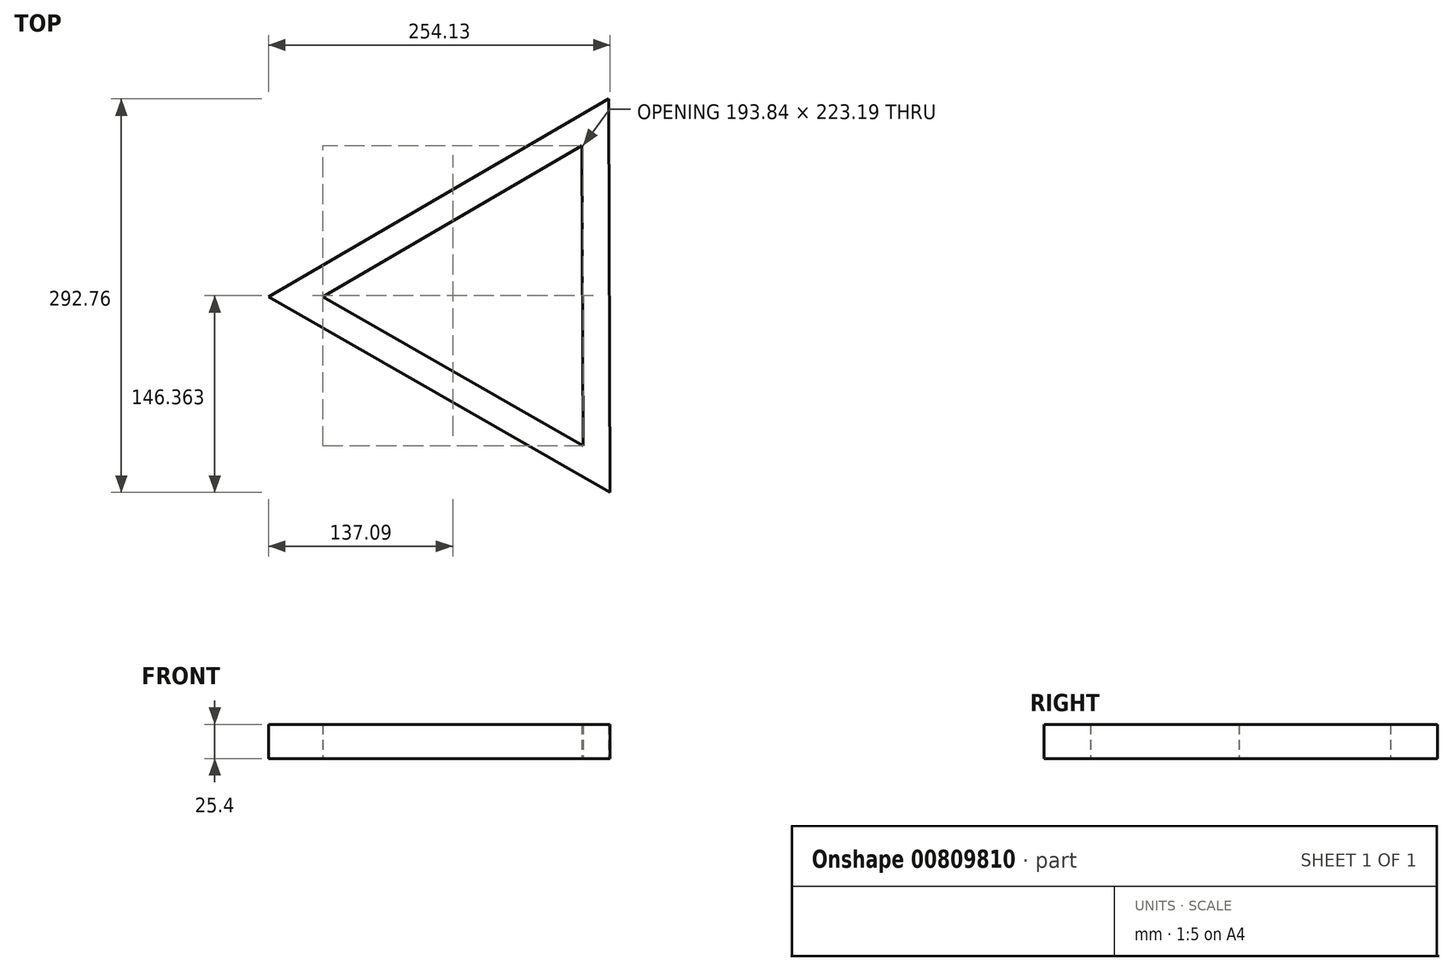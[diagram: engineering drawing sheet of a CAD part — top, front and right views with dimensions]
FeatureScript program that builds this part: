
annotation { "Feature Type Name" : "Feature", "Feature Type Description" : "" }
export const myFeature = defineFeature(function(context is Context, id is Id, definition is map)
    precondition{}
    {
        {
            var Q0;
            Q0=qCreatedBy(makeId("Top.planeOp"),FACE);
            var sketch = newSketch(context, id + "F0", { "sketchPlane" : qUnion([Q0])});
            skLineSegment(sketch, "E0", {"start": v(53.7, 199.94) * mm, "end": v(53.7, 199.96) * mm});
            skCircle(sketch, "E1.cCircle", {"center": v(-30.82, 53.4) * mm, "radius": 84.51 * mm, "construction": true});
            skLineSegment(sketch, "E1.0", {"start": v(53.1, 200.11) * mm, "end": v(54.28, -92.65) * mm});
            skLineSegment(sketch, "E1.1", {"start": v(54.28, -92.65) * mm, "end": v(-199.85, 52.72) * mm});
            skLineSegment(sketch, "E1.2", {"start": v(-199.85, 52.72) * mm, "end": v(53.1, 200.11) * mm});
            skPoint(sketch, "E1.0.midPoint", {"position": v(53.7, 53.73) * mm});
            skCircle(sketch, "E2.cCircle", {"center": v(-30.82, 53.4) * mm, "radius": 64.43 * mm, "construction": true});
            skLineSegment(sketch, "E2.0", {"start": v(33.05, 165.3) * mm, "end": v(34.16, -57.88) * mm});
            skLineSegment(sketch, "E2.1", {"start": v(34.16, -57.88) * mm, "end": v(-159.68, 52.76) * mm});
            skLineSegment(sketch, "E2.2", {"start": v(-159.68, 52.76) * mm, "end": v(33.05, 165.3) * mm});
            skPoint(sketch, "E2.0.midPoint", {"position": v(33.6, 53.71) * mm});
            skSolve(sketch);
        }
        {
            var Q0;
            Q0=qSketchRegion(id+"F0",true);
            extrude(context, id + "F1", {"entities" : qUnion([Q0]), "depth" : 25.4 * mm, "offsetDistance" : 25.4 * mm});
        }
    });
